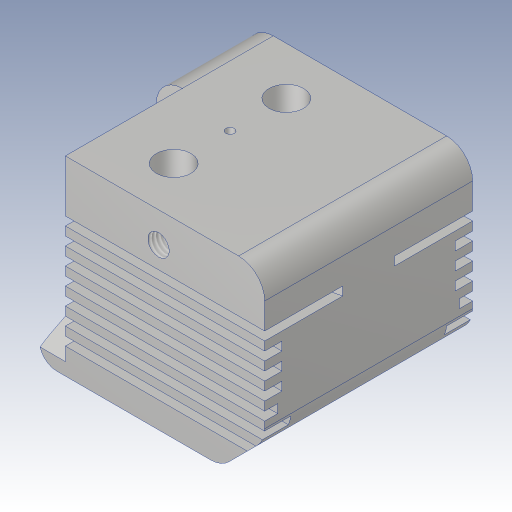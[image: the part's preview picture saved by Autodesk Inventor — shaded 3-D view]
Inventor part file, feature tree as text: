
AUTODESK INVENTOR PART (.ipt)
format: ipt  version: 2023.3 (Build 273359000, 359)  size: 592,384 bytes
history: native  units: in
note: dims shown in document units (in); Inventor stores cm internally (conversion verified against a paired STEP export)
features: sketch x9, hole x7, extrude x4, fillet x2, chamfer x2, mirror x1, projected_geometry x1
ambient origin geometry x8: Origin, YZ Plane, XZ Plane, XY Plane, X Axis, Y Axis, Z Axis, Center Point
bodies: Body1 (feature_tree)
feature tree (26):
  extrude  "Extrusion7"  Depth=1.0236in
  sketch  "Skizze25"  dims[d206=0.0937in d207=0.2362in d208=0.1575in d209=0.0787in d210=90.0deg d211=0.1969in d212=0.0in]
  hole  "Bohrung19"  [1 undecoded]
  fillet  "Rundung3"  Radius=0.4724in
  sketch  "Skizze23"  dims[d125=0.9449in d126=0.0in d203=0.1181in d204=0.4724in]
  hole  "Bohrung16"  [1 undecoded]
  hole  "Bohrung18"  [1 undecoded]
  extrude  "Extrusion10"  Depth=0.315in
  hole  "Bohrung22"  [1 undecoded]
  hole  "Bohrung28"  [1 undecoded]
  fillet  "Rundung14"  Radius=0.0394in
  sketch  "Skizze31"  dims[d226=0.0787in d227=0.2756in d228=0.1575in d229=0.5118in d230=90.0deg d231=0.315in d232=0.8108in d233=0.3937in]
  sketch  "Skizze34"  dims[d234=0.0394in d235=0.2362in d236=0.1575in d237=0.0787in d238=90.0deg d239=0.2756in d240=0.0in d248=0.3937in]
  hole  "Bohrung27"  [1 undecoded]
  hole  "Bohrung26"  [1 undecoded]
  extrude  "Extrusion12"  Depth=0.2559in
  mirror  "Spiegeln1"
  chamfer  "Fase7"  Distance=0.374in
  chamfer  "Fase8"  Distance=0.1772in
  extrude  "Extrusion13"  Depth=0.2461in
  sketch  "Skizze14"  dims[d122=0.8661in d123=1.0236in]
  sketch  "Skizze24"  dims[d205=0.5118in]
  projected_geometry  "Projizierte Kontur6"
  sketch  "Skizze36"  dims[d321=0.0394in d322=0.0394in d323=0.0394in d324=0.0394in d325=0.0394in]
  sketch  "Skizze37"  dims[d328=0.0394in d329=0.0394in d330=0.0394in d331=0.0394in d332=0.0394in]
  sketch  "Skizze38"  dims[d335=0.0394in d336=0.0394in d337=0.0394in d338=0.0394in d339=0.0394in d342=0.0394in d343=0.0394in d344=0.0394in d345=0.0394in d346=0.0394in d384=0.315in d386=0.3937in d387=0.6496in d388=0.0in d389=0.0394in d425=0.0787in d426=0.5118in d427=0.2559in d428=0.374in d429=0.1772in d431=0.2461in d432=0.1181in d433=0.2362in d434=0.1575in d435=0.5118in d436=90.0deg d437=0.315in d438=0.0in d482=0.0787in d484=0.1378in d485=0.5118in d493=0.0512in d494=0.0512in d495=0.0512in d496=0.0512in d497=0.2756in d498=0.0394in d499=0.1181in d500=0.0394in d501=0.0394in d502=0.0787in d503=0.0394in d504=0.0787in d505=0.0394in d506=0.0394in d507=0.0787in d508=0.0394in d509=0.1181in d511=0.0394in d513=0.3937in d514=0.0in d515=0.0394in d516=0.0591in d517=0.0394in d518=0.0394in d519=0.0394in d520=0.1181in d521=0.0394in d522=0.0787in d523=0.3543in d524=45.0deg d525=0.0787in d526=0.315in d527=45.0deg d528=0.374in d529=0.187in d530=0.1181in d531=0.315in d533=0.1855in d534=0.5118in d535=0.1181in d536=0.1181in d537=0.1575in d538=0.1575in d539=0.1181in d540=0.0in d541=0.1855in d542=0.1181in d543=0.3937in d544=0.0394in d545=0.2559in d546=0.0968in d547=0.2362in d548=0.248in d549=0.0787in d550=90.0deg d551=0.3465in d552=0.0in d553=0.0968in d554=0.2362in d555=0.1575in d556=0.0787in d557=90.0deg d558=0.3465in d559=0.0in d560=0.5413in d562=45.0deg d563=0.1969in d564=0.1181in d565=0.1575in d566=0.0787in d567=0.0787in d568=0.0512in d569=0.0512in d570=0.0512in d571=0.0512in d573=0.1181in d574=0.1575in d575=0.1575in d576=0.1181in d577=0.2362in d578=0.1575in d579=0.5118in d580=90.0deg d581=0.315in d582=0.0in d394=0.0197in d395=0.0344in d396=0.0197in d397=0.0344in d404=0.0197in d405=0.0344in d406=0.0197in d407=0.0344in d561=0.0in d572=0.0098in]
note: 7 required parameter values undecoded (feature->parameter linkage not recoverable at this tier; creation-order binding heuristic only, values carry confidence <= 0.55)
